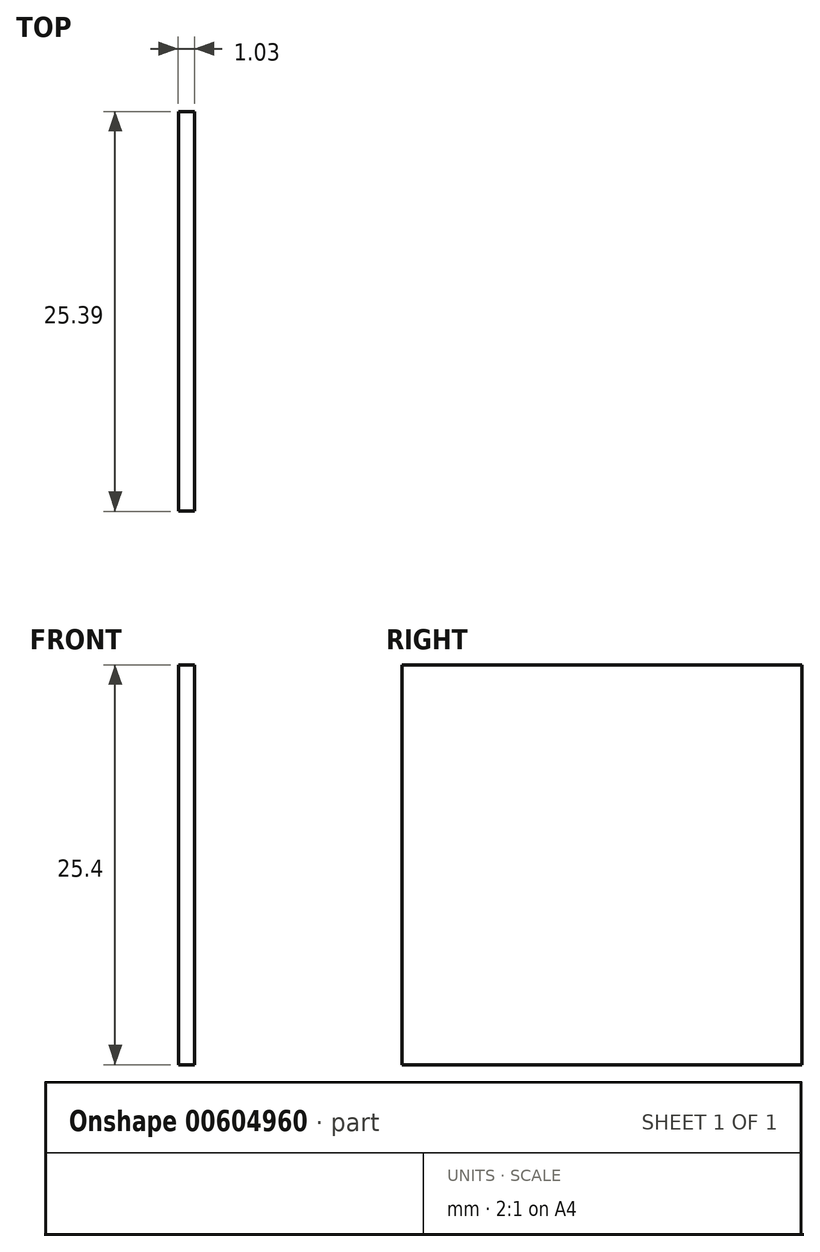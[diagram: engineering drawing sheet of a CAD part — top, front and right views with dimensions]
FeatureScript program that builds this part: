
annotation { "Feature Type Name" : "Feature", "Feature Type Description" : "" }
export const myFeature = defineFeature(function(context is Context, id is Id, definition is map)
    precondition{}
    {
        {
            var Q0;
            Q0=qCreatedBy(makeId("Top.planeOp"),FACE);
            var sketch = newSketch(context, id + "F0", { "sketchPlane" : qUnion([Q0])});
            skLineSegment(sketch, "E0.bottom", {"start": v(-40.65, 22.44) * mm, "end": v(-39.62, 22.44) * mm});
            skLineSegment(sketch, "E0.top", {"start": v(-40.65, -2.95) * mm, "end": v(-39.62, -2.95) * mm});
            skLineSegment(sketch, "E0.left", {"start": v(-40.65, 22.44) * mm, "end": v(-40.65, -2.95) * mm});
            skLineSegment(sketch, "E0.right", {"start": v(-39.62, 22.44) * mm, "end": v(-39.62, -2.95) * mm});
            skSolve(sketch);
        }
        {
            var Q0;
            Q0=makeQuery(id+"F0.imprint","IMPRINT",FACE,{"disambiguationData":[TD([[makeQuery(id+"F0.imprint","IMPRINT",EDGE,{"derivedFrom":sQuery(id+"F0.wireOp",EDGE,"E0.bottom")}),-1.0]])]});
            extrude(context, id + "F1", {"entities" : qUnion([Q0]), "depth" : 25.4 * mm, "offsetDistance" : 25.4 * mm});
        }
    });
